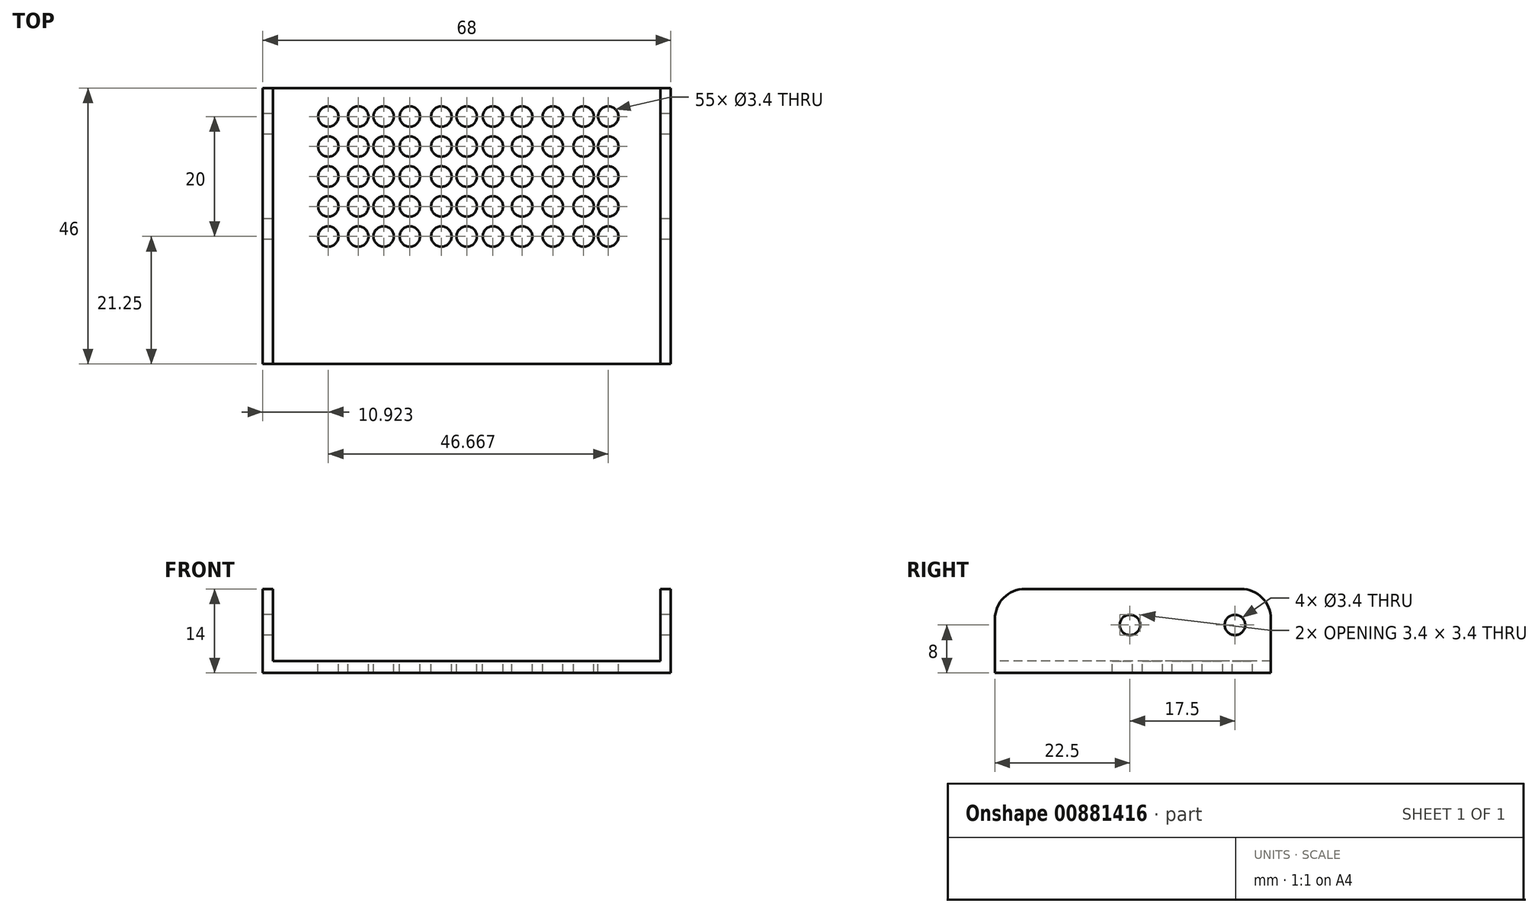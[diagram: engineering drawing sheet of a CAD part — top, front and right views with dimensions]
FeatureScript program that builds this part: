
annotation { "Feature Type Name" : "Feature", "Feature Type Description" : "" }
export const myFeature = defineFeature(function(context is Context, id is Id, definition is map)
    precondition{}
    {
        {
            var Q0;
            Q0=qCreatedBy(makeId("Top.planeOp"),FACE);
            var sketch = newSketch(context, id + "F0", { "sketchPlane" : qUnion([Q0])});
            skLineSegment(sketch, "E0.bottom", {"start": v(34, -14.75) * mm, "end": v(-34, -14.75) * mm});
            skLineSegment(sketch, "E0.top", {"start": v(34, 14.75) * mm, "end": v(-34, 14.75) * mm});
            skLineSegment(sketch, "E0.left", {"start": v(34, -14.75) * mm, "end": v(34, 14.75) * mm});
            skLineSegment(sketch, "E0.right", {"start": v(-34, -14.75) * mm, "end": v(-34, 14.75) * mm});
            skPoint(sketch, "E0.middle", {"position": v(0, 0) * mm});
            skSolve(sketch);
        }
        {
            var Q0;
            Q0=makeQuery(id+"F0.imprint","IMPRINT",FACE,{"disambiguationData":[TD([[makeQuery(id+"F0.imprint","IMPRINT",EDGE,{"derivedFrom":sQuery(id+"F0.wireOp",EDGE,"E0.bottom")}),-1.0]])]});
            extrude(context, id + "F1", {"entities" : qUnion([Q0]), "depth" : 2 * mm, "offsetDistance" : 25 * mm});
        }
        {
            var Q0;
            Q0=makeQuery(id+"F1.opExtrude","CAP_FACE",FACE,{"disambiguationData":[OSD([sQuery(id+"F0.wireOp",EDGE,"E0.bottom"),sQuery(id+"F0.wireOp",EDGE,"E0.top"),sQuery(id+"F0.wireOp",EDGE,"E0.left"),sQuery(id+"F0.wireOp",EDGE,"E0.right")])],"isStart":false});
            var sketch = newSketch(context, id + "F2", { "sketchPlane" : qUnion([Q0])});
            skPoint(sketch, "E1", {"position": v(-32.1, 14.75) * mm});
            skPoint(sketch, "E2", {"position": v(-32.1, -14.75) * mm});
            skPoint(sketch, "E3", {"position": v(32.1, -14.75) * mm});
            skPoint(sketch, "E4", {"position": v(32.1, 14.75) * mm});
            skLineSegment(sketch, "E5", {"start": v(-32.1, 14.75) * mm, "end": v(-32.1, -14.75) * mm});
            skLineSegment(sketch, "E6", {"start": v(32.1, 14.75) * mm, "end": v(32.1, -14.75) * mm});
            skSolve(sketch);
        }
        {
            var Q0;
            {var subQ0=sQuery(id+"F2.wireOp",EDGE,"E5");Q0=makeQuery(id+"F2.imprint","IMPRINT",FACE,{"disambiguationData":[TD([[makeQuery(id+"F2.imprint","IMPRINT",EDGE,{"derivedFrom":subQ0}),-1.0]])]});}
            var Q1;
            {var subQ0=sQuery(id+"F2.wireOp",EDGE,"E6");Q1=makeQuery(id+"F2.imprint","IMPRINT",FACE,{"disambiguationData":[TD([[makeQuery(id+"F2.imprint","IMPRINT",EDGE,{"derivedFrom":subQ0}),1.0]])]});}
            extrude(context, id + "F3", {"entities" : qUnion([Q0, Q1]), "operationType" : NewBodyOperationType.ADD, "depth" : 12 * mm, "offsetDistance" : 25 * mm});
        }
        {
            var Q0;
            {var subQ0=sQuery(id+"F0.wireOp",EDGE,"E0.left");Q0=makeQuery(id+"F3.boolean.opBoolean","MERGE",FACE,{"derivedFrom":[makeQuery(id+"F1.opExtrude","SWEPT_FACE",FACE,{"disambiguationData":[OSD([subQ0])]}),makeQuery(id+"F3.opExtrude","SWEPT_FACE",FACE,{"disambiguationData":[OSD([subQ0])]})]});}
            var sketch = newSketch(context, id + "F4", { "sketchPlane" : qUnion([Q0])});
            skPoint(sketch, "E7", {"position": v(-8.75, 8) * mm});
            skPoint(sketch, "E8", {"position": v(8.75, 8) * mm});
            skSolve(sketch);
        }
        {
            var Q0;
            Q0=sQuery(id+"F4.wireOp",VERTEX,"E7");
            var Q1;
            Q1=sQuery(id+"F4.wireOp",VERTEX,"E8");
            var Q2;
            Q2=makeQuery(id+"F1.opExtrude","SWEPT_BODY",BODY,{"disambiguationData":[OSD([sQuery(id+"F0.wireOp",EDGE,"E0.bottom"),sQuery(id+"F0.wireOp",EDGE,"E0.top"),sQuery(id+"F0.wireOp",EDGE,"E0.left"),sQuery(id+"F0.wireOp",EDGE,"E0.right")])]});
            hole(context, id + "F5", {"style" : HoleStyle.SIMPLE, "endStyle" : HoleEndStyle.THROUGH, "standardTappedOrClearance" : lookupTablePath({ "fit" : "Normal", "standard" : "ISO", "size" : "M3", "type" : "Clearance" }), "standardBlindInLast" : lookupTablePath({ "fit" : "Normal", "standard" : "ISO", "engagement" : "75%", "pitch" : "0.5 mm", "size" : "M3", "type" : "Clearance & tapped" }), "holeDiameter" : 3.4 * mm, "majorDiameter" : 5 * mm, "isTappedThrough" : true, "tappedDepth" : 12 * mm, "tapClearance" : 3, "locations" : qUnion([Q0, Q1]), "scope" : qUnion([Q2]), "startStyle" : HoleStartStyle.SKETCH});
        }
        {
            var Q0;
            Q0=makeQuery(id+"F1.opExtrude","CAP_FACE",FACE,{"disambiguationData":[OSD([sQuery(id+"F0.wireOp",EDGE,"E0.bottom"),sQuery(id+"F0.wireOp",EDGE,"E0.top"),sQuery(id+"F0.wireOp",EDGE,"E0.left"),sQuery(id+"F0.wireOp",EDGE,"E0.right")])],"isStart":true});
            var sketch = newSketch(context, id + "F6", { "sketchPlane" : qUnion([Q0])});
            skPoint(sketch, "E9", {"position": v(0, 0) * mm});
            skPoint(sketch, "E10", {"position": v(0, 5) * mm});
            skPoint(sketch, "E11", {"position": v(0, 10) * mm});
            skPoint(sketch, "E12", {"position": v(0, -5) * mm});
            skPoint(sketch, "E13", {"position": v(0, -10) * mm});
            skPoint(sketch, "E14", {"position": v(4.36, -10) * mm});
            skPoint(sketch, "E15", {"position": v(9.23, -10) * mm});
            skPoint(sketch, "E16", {"position": v(14.36, -10) * mm});
            skPoint(sketch, "E17", {"position": v(19.49, -10) * mm});
            skPoint(sketch, "E18", {"position": v(23.59, -10) * mm});
            skPoint(sketch, "E19", {"position": v(-4.23, -10) * mm});
            skPoint(sketch, "E20", {"position": v(-9.49, -10) * mm});
            skPoint(sketch, "E21", {"position": v(-13.85, -10) * mm});
            skPoint(sketch, "E22", {"position": v(-18.08, -10) * mm});
            skPoint(sketch, "E23", {"position": v(-23.08, -10) * mm});
            skPoint(sketch, "E24", {"position": v(-4.23, -5) * mm});
            skPoint(sketch, "E25", {"position": v(-9.49, -5) * mm});
            skPoint(sketch, "E26", {"position": v(-13.85, -5) * mm});
            skPoint(sketch, "E27", {"position": v(-18.08, -5) * mm});
            skPoint(sketch, "E28", {"position": v(-23.08, -5) * mm});
            skPoint(sketch, "E29", {"position": v(-23.08, 0) * mm});
            skPoint(sketch, "E30", {"position": v(-18.08, 0) * mm});
            skPoint(sketch, "E31", {"position": v(-13.85, 0) * mm});
            skPoint(sketch, "E32", {"position": v(-9.49, 0) * mm});
            skPoint(sketch, "E33", {"position": v(-4.23, 0) * mm});
            skPoint(sketch, "E34", {"position": v(-23.08, 5) * mm});
            skPoint(sketch, "E35", {"position": v(-18.08, 5) * mm});
            skPoint(sketch, "E36", {"position": v(-13.85, 5) * mm});
            skPoint(sketch, "E37", {"position": v(-9.49, 5) * mm});
            skPoint(sketch, "E38", {"position": v(-4.23, 5) * mm});
            skPoint(sketch, "E39", {"position": v(-23.08, 10) * mm});
            skPoint(sketch, "E40", {"position": v(-18.08, 10) * mm});
            skPoint(sketch, "E41", {"position": v(-13.85, 10) * mm});
            skPoint(sketch, "E42", {"position": v(-9.49, 10) * mm});
            skPoint(sketch, "E43", {"position": v(-4.23, 10) * mm});
            skPoint(sketch, "E44", {"position": v(23.59, 10) * mm});
            skPoint(sketch, "E45", {"position": v(23.59, 5) * mm});
            skPoint(sketch, "E46", {"position": v(23.59, 0) * mm});
            skPoint(sketch, "E47", {"position": v(23.59, -5) * mm});
            skPoint(sketch, "E48", {"position": v(19.49, -5) * mm});
            skPoint(sketch, "E49", {"position": v(19.49, 0) * mm});
            skPoint(sketch, "E50", {"position": v(19.49, 5) * mm});
            skPoint(sketch, "E51", {"position": v(19.49, 10) * mm});
            skPoint(sketch, "E52", {"position": v(14.36, -5) * mm});
            skPoint(sketch, "E53", {"position": v(14.36, 0) * mm});
            skPoint(sketch, "E54", {"position": v(14.36, 5) * mm});
            skPoint(sketch, "E55", {"position": v(14.36, 10) * mm});
            skPoint(sketch, "E56", {"position": v(9.23, -5) * mm});
            skPoint(sketch, "E57", {"position": v(9.23, 0) * mm});
            skPoint(sketch, "E58", {"position": v(9.23, 5) * mm});
            skPoint(sketch, "E59", {"position": v(9.23, 10) * mm});
            skPoint(sketch, "E60", {"position": v(4.36, -5) * mm});
            skPoint(sketch, "E61", {"position": v(4.36, 0) * mm});
            skPoint(sketch, "E62", {"position": v(4.36, 5) * mm});
            skPoint(sketch, "E63", {"position": v(4.36, 10) * mm});
            skSolve(sketch);
        }
        {
            var Q0;
            Q0=sQuery(id+"F6.wireOp",VERTEX,"E23");
            var Q1;
            Q1=sQuery(id+"F6.wireOp",VERTEX,"E22");
            var Q2;
            Q2=sQuery(id+"F6.wireOp",VERTEX,"E21");
            var Q3;
            Q3=sQuery(id+"F6.wireOp",VERTEX,"E20");
            var Q4;
            Q4=sQuery(id+"F6.wireOp",VERTEX,"E19");
            var Q5;
            Q5=sQuery(id+"F6.wireOp",VERTEX,"E13");
            var Q6;
            Q6=sQuery(id+"F6.wireOp",VERTEX,"E14");
            var Q7;
            Q7=sQuery(id+"F6.wireOp",VERTEX,"E15");
            var Q8;
            Q8=sQuery(id+"F6.wireOp",VERTEX,"E16");
            var Q9;
            Q9=sQuery(id+"F6.wireOp",VERTEX,"E17");
            var Q10;
            Q10=sQuery(id+"F6.wireOp",VERTEX,"E18");
            var Q11;
            Q11=sQuery(id+"F6.wireOp",VERTEX,"E47");
            var Q12;
            Q12=sQuery(id+"F6.wireOp",VERTEX,"E48");
            var Q13;
            Q13=sQuery(id+"F6.wireOp",VERTEX,"E52");
            var Q14;
            Q14=sQuery(id+"F6.wireOp",VERTEX,"E56");
            var Q15;
            Q15=sQuery(id+"F6.wireOp",VERTEX,"E60");
            var Q16;
            Q16=sQuery(id+"F6.wireOp",VERTEX,"E12");
            var Q17;
            Q17=sQuery(id+"F6.wireOp",VERTEX,"E24");
            var Q18;
            Q18=sQuery(id+"F6.wireOp",VERTEX,"E25");
            var Q19;
            Q19=sQuery(id+"F6.wireOp",VERTEX,"E26");
            var Q20;
            Q20=sQuery(id+"F6.wireOp",VERTEX,"E27");
            var Q21;
            Q21=sQuery(id+"F6.wireOp",VERTEX,"E28");
            var Q22;
            Q22=sQuery(id+"F6.wireOp",VERTEX,"E29");
            var Q23;
            Q23=sQuery(id+"F6.wireOp",VERTEX,"E30");
            var Q24;
            Q24=sQuery(id+"F6.wireOp",VERTEX,"E31");
            var Q25;
            Q25=sQuery(id+"F6.wireOp",VERTEX,"E32");
            var Q26;
            Q26=sQuery(id+"F6.wireOp",VERTEX,"E33");
            var Q27;
            Q27=sQuery(id+"F6.wireOp",VERTEX,"E9");
            var Q28;
            Q28=sQuery(id+"F6.wireOp",VERTEX,"E53");
            var Q29;
            Q29=sQuery(id+"F6.wireOp",VERTEX,"E61");
            var Q30;
            Q30=sQuery(id+"F6.wireOp",VERTEX,"E57");
            var Q31;
            Q31=sQuery(id+"F6.wireOp",VERTEX,"E49");
            var Q32;
            Q32=sQuery(id+"F6.wireOp",VERTEX,"E46");
            var Q33;
            Q33=sQuery(id+"F6.wireOp",VERTEX,"E45");
            var Q34;
            Q34=sQuery(id+"F6.wireOp",VERTEX,"E50");
            var Q35;
            Q35=sQuery(id+"F6.wireOp",VERTEX,"E54");
            var Q36;
            Q36=sQuery(id+"F6.wireOp",VERTEX,"E58");
            var Q37;
            Q37=sQuery(id+"F6.wireOp",VERTEX,"E62");
            var Q38;
            Q38=sQuery(id+"F6.wireOp",VERTEX,"E10");
            var Q39;
            Q39=sQuery(id+"F6.wireOp",VERTEX,"E38");
            var Q40;
            Q40=sQuery(id+"F6.wireOp",VERTEX,"E37");
            var Q41;
            Q41=sQuery(id+"F6.wireOp",VERTEX,"E36");
            var Q42;
            Q42=sQuery(id+"F6.wireOp",VERTEX,"E35");
            var Q43;
            Q43=sQuery(id+"F6.wireOp",VERTEX,"E34");
            var Q44;
            Q44=sQuery(id+"F6.wireOp",VERTEX,"E39");
            var Q45;
            Q45=sQuery(id+"F6.wireOp",VERTEX,"E40");
            var Q46;
            Q46=sQuery(id+"F6.wireOp",VERTEX,"E41");
            var Q47;
            Q47=sQuery(id+"F6.wireOp",VERTEX,"E42");
            var Q48;
            Q48=sQuery(id+"F6.wireOp",VERTEX,"E43");
            var Q49;
            Q49=sQuery(id+"F6.wireOp",VERTEX,"E11");
            var Q50;
            Q50=sQuery(id+"F6.wireOp",VERTEX,"E63");
            var Q51;
            Q51=sQuery(id+"F6.wireOp",VERTEX,"E59");
            var Q52;
            Q52=sQuery(id+"F6.wireOp",VERTEX,"E55");
            var Q53;
            Q53=sQuery(id+"F6.wireOp",VERTEX,"E51");
            var Q54;
            Q54=sQuery(id+"F6.wireOp",VERTEX,"E44");
            var Q55;
            Q55=makeQuery(id+"F1.opExtrude","SWEPT_BODY",BODY,{"disambiguationData":[OSD([sQuery(id+"F0.wireOp",EDGE,"E0.bottom"),sQuery(id+"F0.wireOp",EDGE,"E0.top"),sQuery(id+"F0.wireOp",EDGE,"E0.left"),sQuery(id+"F0.wireOp",EDGE,"E0.right")])]});
            hole(context, id + "F7", {"style" : HoleStyle.SIMPLE, "endStyle" : HoleEndStyle.THROUGH, "standardTappedOrClearance" : lookupTablePath({ "fit" : "Normal", "standard" : "ISO", "size" : "M3", "type" : "Clearance" }), "standardBlindInLast" : lookupTablePath({ "fit" : "Normal", "standard" : "ISO", "engagement" : "75%", "pitch" : "0.5 mm", "size" : "M3", "type" : "Clearance & tapped" }), "holeDiameter" : 3.4 * mm, "majorDiameter" : 5 * mm, "isTappedThrough" : true, "tappedDepth" : 12 * mm, "tapClearance" : 3, "locations" : qUnion([Q0, Q1, Q2, Q3, Q4, Q5, Q6, Q7, Q8, Q9, Q10, Q11, Q12, Q13, Q14, Q15, Q16, Q17, Q18, Q19, Q20, Q21, Q22, Q23, Q24, Q25, Q26, Q27, Q28, Q29, Q30, Q31, Q32, Q33, Q34, Q35, Q36, Q37, Q38, Q39, Q40, Q41, Q42, Q43, Q44, Q45, Q46, Q47, Q48, Q49, Q50, Q51, Q52, Q53, Q54]), "scope" : qUnion([Q55]), "startStyle" : HoleStartStyle.SKETCH});
        }
        {
            var Q0;
            {var subQ0=sQuery(id+"F0.wireOp",EDGE,"E0.bottom");var subQ1=makeQuery(id+"F1.opExtrude","CAP_EDGE",EDGE,{"disambiguationData":[OSD([subQ0])],"isStart":false});Q0=makeQuery(id+"F3.boolean.opBoolean","MERGE",FACE,{"derivedFrom":[makeQuery(id+"F1.opExtrude","SWEPT_FACE",FACE,{"disambiguationData":[OSD([subQ0])]}),makeQuery(id+"F3.opExtrude","SWEPT_FACE",FACE,{"disambiguationData":[OSD([subQ0]),TDD([makeQuery(id+"F2.imprint","IMPRINT",EDGE,{"disambiguationData":[TD([[makeQuery(id+"F2.imprint","INTERSECT",VERTEX,{"derivedFrom":[subQ1,makeQuery(id+"F1.opExtrude","CAP_EDGE",EDGE,{"disambiguationData":[OSD([sQuery(id+"F0.wireOp",EDGE,"E0.left")])],"isStart":false})]}),-1.0]])],"derivedFrom":subQ1})])]}),makeQuery(id+"F3.opExtrude","SWEPT_FACE",FACE,{"disambiguationData":[OSD([subQ0]),TDD([makeQuery(id+"F2.imprint","IMPRINT",EDGE,{"disambiguationData":[TD([[makeQuery(id+"F2.imprint","INTERSECT",VERTEX,{"derivedFrom":[subQ1,makeQuery(id+"F1.opExtrude","CAP_EDGE",EDGE,{"disambiguationData":[OSD([sQuery(id+"F0.wireOp",EDGE,"E0.right")])],"isStart":false})]}),1.0]])],"derivedFrom":subQ1})])]})]});}
            extrude(context, id + "F8", {"entities" : qUnion([Q0]), "operationType" : NewBodyOperationType.ADD, "depth" : 16.5 * mm, "offsetDistance" : 25 * mm});
        }
        {
            var Q0;
            {var subQ0=sQuery(id+"F2.wireOp",EDGE,"E5");Q0=makeQuery(id+"F8.boolean.opBoolean","MERGE",FACE,{"derivedFrom":[makeQuery(id+"F3.opExtrude","SWEPT_FACE",FACE,{"disambiguationData":[OSD([subQ0])]}),makeQuery(id+"F8.opExtrude","SWEPT_FACE",FACE,{"disambiguationData":[OSD([sQuery(id+"F0.wireOp",EDGE,"E0.bottom"),subQ0])]})]});}
            extrude(context, id + "F9", {"entities" : qUnion([Q0]), "operationType" : NewBodyOperationType.REMOVE, "oppositeDirection" : true, "depth" : 0.2 * mm, "offsetDistance" : 25 * mm});
        }
        {
            var Q0;
            {var subQ0=sQuery(id+"F2.wireOp",EDGE,"E6");Q0=makeQuery(id+"F8.boolean.opBoolean","MERGE",FACE,{"derivedFrom":[makeQuery(id+"F3.opExtrude","SWEPT_FACE",FACE,{"disambiguationData":[OSD([subQ0])]}),makeQuery(id+"F8.opExtrude","SWEPT_FACE",FACE,{"disambiguationData":[OSD([sQuery(id+"F0.wireOp",EDGE,"E0.bottom"),subQ0])]})]});}
            extrude(context, id + "F10", {"entities" : qUnion([Q0]), "operationType" : NewBodyOperationType.REMOVE, "oppositeDirection" : true, "depth" : 0.2 * mm, "offsetDistance" : 25 * mm});
        }
        {
            var Q0;
            {var subQ0=sQuery(id+"F0.wireOp",EDGE,"E0.bottom");var subQ1=makeQuery(id+"F1.opExtrude","CAP_EDGE",EDGE,{"disambiguationData":[OSD([subQ0])],"isStart":false});Q0=makeQuery(id+"F8.opExtrude","CAP_EDGE",EDGE,{"disambiguationData":[OSD([subQ0]),TDD([makeQuery(id+"F3.opExtrude","CAP_EDGE",EDGE,{"disambiguationData":[OSD([subQ0]),TDD([makeQuery(id+"F2.imprint","IMPRINT",EDGE,{"disambiguationData":[TD([[makeQuery(id+"F2.imprint","INTERSECT",VERTEX,{"derivedFrom":[subQ1,makeQuery(id+"F1.opExtrude","CAP_EDGE",EDGE,{"disambiguationData":[OSD([sQuery(id+"F0.wireOp",EDGE,"E0.right")])],"isStart":false})]}),1.0]])],"derivedFrom":subQ1})])],"isStart":false})])],"isStart":false});}
            var Q1;
            {var subQ0=sQuery(id+"F0.wireOp",EDGE,"E0.bottom");var subQ1=makeQuery(id+"F1.opExtrude","CAP_EDGE",EDGE,{"disambiguationData":[OSD([subQ0])],"isStart":false});Q1=makeQuery(id+"F8.opExtrude","CAP_EDGE",EDGE,{"disambiguationData":[OSD([subQ0]),TDD([makeQuery(id+"F3.opExtrude","CAP_EDGE",EDGE,{"disambiguationData":[OSD([subQ0]),TDD([makeQuery(id+"F2.imprint","IMPRINT",EDGE,{"disambiguationData":[TD([[makeQuery(id+"F2.imprint","INTERSECT",VERTEX,{"derivedFrom":[subQ1,makeQuery(id+"F1.opExtrude","CAP_EDGE",EDGE,{"disambiguationData":[OSD([sQuery(id+"F0.wireOp",EDGE,"E0.left")])],"isStart":false})]}),-1.0]])],"derivedFrom":subQ1})])],"isStart":false})])],"isStart":false});}
            var Q2;
            {var subQ0=sQuery(id+"F0.wireOp",EDGE,"E0.top");var subQ1=makeQuery(id+"F1.opExtrude","CAP_EDGE",EDGE,{"disambiguationData":[OSD([subQ0])],"isStart":false});Q2=makeQuery(id+"F3.opExtrude","CAP_EDGE",EDGE,{"disambiguationData":[OSD([subQ0]),TDD([makeQuery(id+"F2.imprint","IMPRINT",EDGE,{"disambiguationData":[TD([[makeQuery(id+"F2.imprint","INTERSECT",VERTEX,{"derivedFrom":[subQ1,makeQuery(id+"F1.opExtrude","CAP_EDGE",EDGE,{"disambiguationData":[OSD([sQuery(id+"F0.wireOp",EDGE,"E0.right")])],"isStart":false})]}),1.0]])],"derivedFrom":subQ1})])],"isStart":false});}
            var Q3;
            {var subQ0=sQuery(id+"F0.wireOp",EDGE,"E0.top");var subQ1=makeQuery(id+"F1.opExtrude","CAP_EDGE",EDGE,{"disambiguationData":[OSD([subQ0])],"isStart":false});Q3=makeQuery(id+"F3.opExtrude","CAP_EDGE",EDGE,{"disambiguationData":[OSD([subQ0]),TDD([makeQuery(id+"F2.imprint","IMPRINT",EDGE,{"disambiguationData":[TD([[makeQuery(id+"F2.imprint","INTERSECT",VERTEX,{"derivedFrom":[subQ1,makeQuery(id+"F1.opExtrude","CAP_EDGE",EDGE,{"disambiguationData":[OSD([sQuery(id+"F0.wireOp",EDGE,"E0.left")])],"isStart":false})]}),-1.0]])],"derivedFrom":subQ1})])],"isStart":false});}
            fillet(context, id + "F11", {"entities" : qUnion([Q0, Q1, Q2, Q3]), "tangentPropagation" : true, "radius" : 5 * mm, "defaultsChanged" : false, "vertexSettings" : [], "allowEdgeOverflow" : false});
        }
    });
